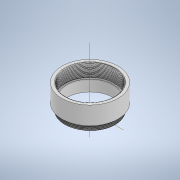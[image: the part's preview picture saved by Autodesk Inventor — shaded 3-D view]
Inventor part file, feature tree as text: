
AUTODESK INVENTOR PART (.ipt)
format: ipt  version: 2020.2 (Build 242310000, 310)  size: 1,705,472 bytes
history: native  units: in
note: dims shown in document units (in); Inventor stores cm internally (conversion verified against a paired STEP export)
features: sketch x6, revolve x4, thread x2, helix x2
ambient origin geometry x8: Origin, YZ Plane, XZ Plane, XY Plane, X Axis, Y Axis, Z Axis, Center Point
bodies: Solid5 (feature_tree), Solid6 (feature_tree)
feature tree (14):
  revolve  "Revolution2"  [1 undecoded]
  thread  "Thread3"  [1 undecoded]
  thread  "Thread4"  [1 undecoded]
  revolve  "Revolution6"  Angle=90.0deg
  helix  "Coil3"  [1 undecoded]
  revolve  "Revolution7"  [1 undecoded]
  revolve  "Revolution8"  [1 undecoded]
  helix  "Coil4"  [1 undecoded]
  sketch  "Sketch2"  dims[d8=0.625in d9=0.561in d10=0.15in d11=0.05in]
  sketch  "Sketch8"  dims[d12=0.1in d13=90.0deg d25=0.3779in]
  sketch  "Sketch9"  dims[d43=0.3779in d55=0.3in]
  sketch  "Sketch10"  dims[d56=0.3in d57=0.0in d58=0.15in d59=0.0in d60=0.3779in d61=0.0038in d62=0.0038in]
  sketch  "Sketch11"  dims[d65=0.0236in]
  sketch  "Sketch12"  dims[d67=0.3779in d69=0.0in d70=0.0236in d71=0.3472in d72=0.3937in d73=0.0in d74=0.0in d75=0.0in d76=0.0in d77=0.0in d78=0.3779in d79=0.0038in d80=0.0038in d83=0.0236in d85=0.3779in d87=0.0in d88=0.0in d89=0.0236in d90=0.1972in d91=0.3937in d92=0.0in d93=0.0in d94=0.0in d95=0.0in d96=0.0in]
note: 7 required parameter values undecoded (feature->parameter linkage not recoverable at this tier; creation-order binding heuristic only, values carry confidence <= 0.55)